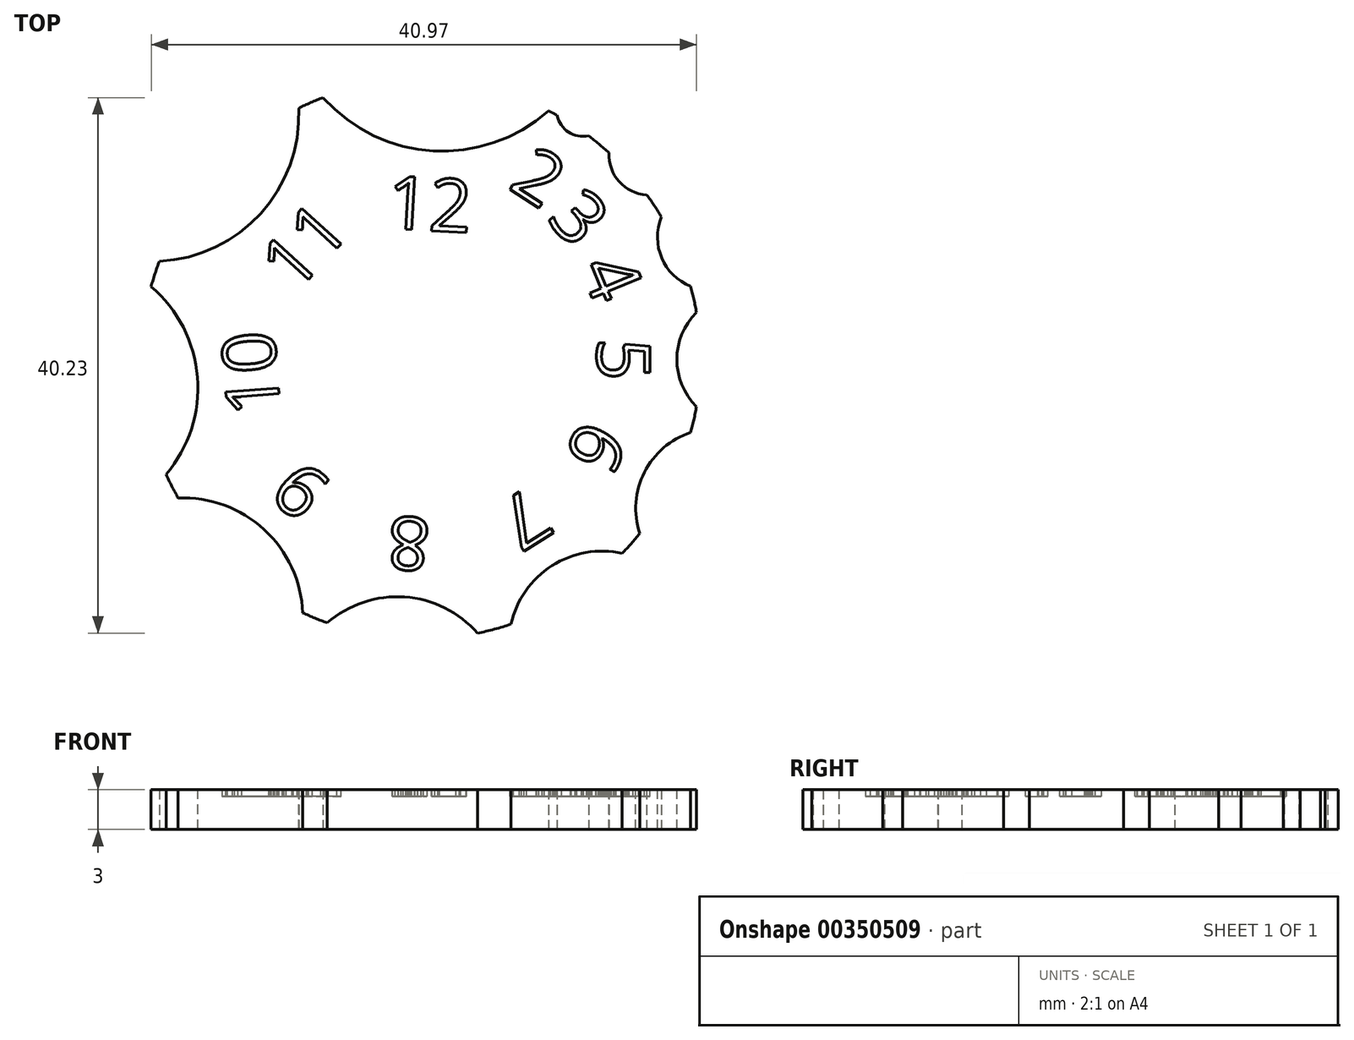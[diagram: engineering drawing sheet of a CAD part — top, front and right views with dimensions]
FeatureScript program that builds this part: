
annotation { "Feature Type Name" : "Feature", "Feature Type Description" : "" }
export const myFeature = defineFeature(function(context is Context, id is Id, definition is map)
    precondition{}
    {
        {
            assignVariable(context, id + "F0", {"name" : "max", "anyValue" : 10});
        }
        {
            var Q0;
            Q0=qCreatedBy(makeId("Top.planeOp"),FACE);
            var sketch = newSketch(context, id + "F1", { "sketchPlane" : qUnion([Q0])});
            skCircle(sketch, "E0", {"center": v(0, 0) * mm, "radius": 21 * mm});
            skSolve(sketch);
        }
        {
            var Q0;
            Q0=qCreatedBy(makeId("Top.planeOp"),FACE);
            var sketch = newSketch(context, id + "F2", { "sketchPlane" : qUnion([Q0])});
            skLineSegment(sketch, "E1", {"start": v(-20.27, 5.47) * mm, "end": v(-20.27, 5.47) * mm});
            skLineSegment(sketch, "E2", {"start": v(-19.15, -8.62) * mm, "end": v(-19.15, -8.62) * mm});
            skPoint(sketch, "E3.visualSharp", {"position": v(-12.66, -1.01) * mm});
            skLineSegment(sketch, "E4", {"start": v(-19.15, -8.62) * mm, "end": v(-18.24, -10.4) * mm});
            skLineSegment(sketch, "E5", {"start": v(-18.24, -10.4) * mm, "end": v(-9.25, -10.04) * mm});
            skLineSegment(sketch, "E6", {"start": v(-9.25, -10.04) * mm, "end": v(-8.88, -19.03) * mm});
            skLineSegment(sketch, "E7", {"start": v(-8.88, -19.03) * mm, "end": v(-7.03, -19.79) * mm});
            skLineSegment(sketch, "E8", {"start": v(-7.03, -19.79) * mm, "end": v(-1, -14.53) * mm});
            skLineSegment(sketch, "E9", {"start": v(-1, -14.53) * mm, "end": v(4.26, -20.56) * mm});
            skLineSegment(sketch, "E10", {"start": v(4.26, -20.56) * mm, "end": v(6.77, -19.88) * mm});
            skLineSegment(sketch, "E11", {"start": v(6.77, -19.88) * mm, "end": v(8.3, -13.05) * mm});
            skLineSegment(sketch, "E12", {"start": v(8.3, -13.05) * mm, "end": v(15.13, -14.57) * mm});
            skLineSegment(sketch, "E13", {"start": v(15.13, -14.57) * mm, "end": v(16.44, -13.06) * mm});
            skLineSegment(sketch, "E14", {"start": v(16.44, -13.06) * mm, "end": v(14.57, -7.36) * mm});
            skLineSegment(sketch, "E15", {"start": v(14.57, -7.36) * mm, "end": v(20.27, -5.49) * mm});
            skLineSegment(sketch, "E16", {"start": v(20.27, -5.49) * mm, "end": v(20.7, -3.54) * mm});
            skLineSegment(sketch, "E17", {"start": v(20.7, -3.54) * mm, "end": v(17.16, 0) * mm});
            skLineSegment(sketch, "E18", {"start": v(17.16, 0) * mm, "end": v(20.7, 3.54) * mm});
            skLineSegment(sketch, "E19", {"start": v(20.7, 3.54) * mm, "end": v(20.27, 5.49) * mm});
            skLineSegment(sketch, "E20", {"start": v(20.27, 5.49) * mm, "end": v(16.56, 7) * mm});
            skLineSegment(sketch, "E21", {"start": v(16.56, 7) * mm, "end": v(18.07, 10.7) * mm});
            skLineSegment(sketch, "E22", {"start": v(18.07, 10.7) * mm, "end": v(18.07, 10.7) * mm});
            skLineSegment(sketch, "E23", {"start": v(18.07, 10.7) * mm, "end": v(16.97, 12.37) * mm});
            skLineSegment(sketch, "E24", {"start": v(16.97, 12.37) * mm, "end": v(13.97, 12.53) * mm});
            skLineSegment(sketch, "E25", {"start": v(13.97, 12.53) * mm, "end": v(14.14, 15.53) * mm});
            skLineSegment(sketch, "E26", {"start": v(14.14, 15.53) * mm, "end": v(12.6, 16.8) * mm});
            skLineSegment(sketch, "E27", {"start": v(12.6, 16.8) * mm, "end": v(10.64, 16.39) * mm});
            skLineSegment(sketch, "E28", {"start": v(10.64, 16.39) * mm, "end": v(10.22, 18.34) * mm});
            skLineSegment(sketch, "E29", {"start": v(-20.27, 5.47) * mm, "end": v(-12.66, -1.01) * mm});
            skLineSegment(sketch, "E30", {"start": v(-12.66, -1.01) * mm, "end": v(-19.15, -8.62) * mm});
            skLineSegment(sketch, "E31", {"start": v(-20.27, 5.47) * mm, "end": v(-26.76, -2.14) * mm});
            skLineSegment(sketch, "E32", {"start": v(-26.76, -2.14) * mm, "end": v(-19.15, -8.62) * mm});
            skLineSegment(sketch, "E33", {"start": v(-18.24, -10.4) * mm, "end": v(-17.87, -19.4) * mm});
            skLineSegment(sketch, "E34", {"start": v(-17.87, -19.4) * mm, "end": v(-8.88, -19.03) * mm});
            skLineSegment(sketch, "E35", {"start": v(-7.03, -19.79) * mm, "end": v(-1.77, -25.82) * mm});
            skLineSegment(sketch, "E36", {"start": v(-1.77, -25.82) * mm, "end": v(4.26, -20.56) * mm});
            skLineSegment(sketch, "E37", {"start": v(6.77, -19.88) * mm, "end": v(13.6, -21.4) * mm});
            skLineSegment(sketch, "E38", {"start": v(13.6, -21.4) * mm, "end": v(15.13, -14.57) * mm});
            skLineSegment(sketch, "E39", {"start": v(16.44, -13.06) * mm, "end": v(22.14, -11.19) * mm});
            skLineSegment(sketch, "E40", {"start": v(22.14, -11.19) * mm, "end": v(20.27, -5.49) * mm});
            skLineSegment(sketch, "E41", {"start": v(20.7, -3.54) * mm, "end": v(24.24, 0) * mm});
            skLineSegment(sketch, "E42", {"start": v(24.24, 0) * mm, "end": v(20.7, 3.54) * mm});
            skLineSegment(sketch, "E43", {"start": v(20.27, 5.49) * mm, "end": v(21.78, 9.2) * mm});
            skLineSegment(sketch, "E44", {"start": v(21.78, 9.2) * mm, "end": v(18.07, 10.7) * mm});
            skLineSegment(sketch, "E45", {"start": v(16.97, 12.37) * mm, "end": v(17.13, 15.37) * mm});
            skLineSegment(sketch, "E46", {"start": v(17.13, 15.37) * mm, "end": v(14.14, 15.53) * mm});
            skLineSegment(sketch, "E47", {"start": v(12.6, 16.8) * mm, "end": v(12.18, 18.76) * mm});
            skLineSegment(sketch, "E48", {"start": v(12.18, 18.76) * mm, "end": v(10.22, 18.34) * mm});
            skLineSegment(sketch, "E49", {"start": v(-20.27, 5.47) * mm, "end": v(-19.66, 7.38) * mm});
            skLineSegment(sketch, "E50.bottom", {"start": v(-19.66, 7.38) * mm, "end": v(-8.67, 7.9) * mm});
            skLineSegment(sketch, "E50.top", {"start": v(-20.18, 18.37) * mm, "end": v(-9.19, 18.88) * mm});
            skLineSegment(sketch, "E50.left", {"start": v(-19.66, 7.38) * mm, "end": v(-20.18, 18.37) * mm});
            skLineSegment(sketch, "E50.right", {"start": v(-8.67, 7.9) * mm, "end": v(-9.19, 18.88) * mm});
            skLineSegment(sketch, "E51", {"start": v(-9.19, 18.88) * mm, "end": v(-7.35, 19.67) * mm});
            skLineSegment(sketch, "E52.bottom", {"start": v(-7.35, 19.67) * mm, "end": v(0.62, 10.7) * mm});
            skLineSegment(sketch, "E52.top", {"start": v(1.61, 27.65) * mm, "end": v(9.6, 18.68) * mm});
            skLineSegment(sketch, "E52.left", {"start": v(-7.35, 19.67) * mm, "end": v(1.61, 27.65) * mm});
            skLineSegment(sketch, "E52.right", {"start": v(0.62, 10.7) * mm, "end": v(9.6, 18.68) * mm});
            skSolve(sketch);
        }
        {
            var Q0;
            Q0 = qSketchRegion(id + "F1", true);
            extrude(context, id + "F3", {"entities" : qUnion([Q0]), "depth" : 3 * mm});
        }
        {
            var Q0;
            Q0 = qSketchRegion(id + "F2", true);
            extrude(context, id + "F4", {"entities" : qUnion([Q0]), "operationType" : NewBodyOperationType.REMOVE, "endBound" : BoundingType.THROUGH_ALL, "depth" : 25 * mm});
        }
        {
            var Q0;
            Q0=makeQuery(id+"F4.boolean.opBoolean","COPY",EDGE,{"derivedFrom":makeQuery(id+"F4.opExtrude","SWEPT_EDGE",EDGE,{"disambiguationData":[OSD([sQuery(id+"F2.wireOp",EDGE,"E29"),sQuery(id+"F2.wireOp",EDGE,"E30")])]})});
            fillet(context, id + "F5", {"entities" : qUnion([Q0]), "radius" : (getVariable(context, 'max')) * mm, "tangentPropagation" : true, "allowEdgeOverflow" : false});
        }
        {
            var Q0;
            Q0=makeQuery(id+"F4.boolean.opBoolean","COPY",EDGE,{"derivedFrom":makeQuery(id+"F4.opExtrude","SWEPT_EDGE",EDGE,{"disambiguationData":[OSD([sQuery(id+"F2.wireOp",EDGE,"E5"),sQuery(id+"F2.wireOp",EDGE,"E6")])]})});
            fillet(context, id + "F6", {"entities" : qUnion([Q0]), "radius" : (getVariable(context, 'max') - 1) * mm, "tangentPropagation" : true, "allowEdgeOverflow" : false});
        }
        {
            var Q0;
            Q0=makeQuery(id+"F4.boolean.opBoolean","COPY",EDGE,{"derivedFrom":makeQuery(id+"F4.opExtrude","SWEPT_EDGE",EDGE,{"disambiguationData":[OSD([sQuery(id+"F2.wireOp",EDGE,"E8"),sQuery(id+"F2.wireOp",EDGE,"E9")])]})});
            fillet(context, id + "F7", {"entities" : qUnion([Q0]), "radius" : (getVariable(context, 'max') - 2) * mm, "tangentPropagation" : true, "allowEdgeOverflow" : false});
        }
        {
            var Q0;
            Q0=makeQuery(id+"F4.boolean.opBoolean","COPY",EDGE,{"derivedFrom":makeQuery(id+"F4.opExtrude","SWEPT_EDGE",EDGE,{"disambiguationData":[OSD([sQuery(id+"F2.wireOp",EDGE,"E11"),sQuery(id+"F2.wireOp",EDGE,"E12")])]})});
            fillet(context, id + "F8", {"entities" : qUnion([Q0]), "radius" : (getVariable(context, 'max') - 3) * mm, "tangentPropagation" : true, "allowEdgeOverflow" : false});
        }
        {
            var Q0;
            Q0=makeQuery(id+"F4.boolean.opBoolean","COPY",EDGE,{"derivedFrom":makeQuery(id+"F4.opExtrude","SWEPT_EDGE",EDGE,{"disambiguationData":[OSD([sQuery(id+"F2.wireOp",EDGE,"E14"),sQuery(id+"F2.wireOp",EDGE,"E15")])]})});
            fillet(context, id + "F9", {"entities" : qUnion([Q0]), "radius" : (getVariable(context, 'max') - 4) * mm, "tangentPropagation" : true, "allowEdgeOverflow" : false});
        }
        {
            var Q0;
            Q0=makeQuery(id+"F4.boolean.opBoolean","COPY",EDGE,{"derivedFrom":makeQuery(id+"F4.opExtrude","SWEPT_EDGE",EDGE,{"disambiguationData":[OSD([sQuery(id+"F2.wireOp",EDGE,"E17"),sQuery(id+"F2.wireOp",EDGE,"E18")])]})});
            fillet(context, id + "F10", {"entities" : qUnion([Q0]), "radius" : (getVariable(context, 'max') - 5) * mm, "tangentPropagation" : true, "allowEdgeOverflow" : false});
        }
        {
            var Q0;
            Q0=makeQuery(id+"F4.boolean.opBoolean","COPY",EDGE,{"derivedFrom":makeQuery(id+"F4.opExtrude","SWEPT_EDGE",EDGE,{"disambiguationData":[OSD([sQuery(id+"F2.wireOp",EDGE,"E20"),sQuery(id+"F2.wireOp",EDGE,"E21")])]})});
            fillet(context, id + "F11", {"entities" : qUnion([Q0]), "radius" : (getVariable(context, 'max') - 6) * mm, "tangentPropagation" : true, "allowEdgeOverflow" : false});
        }
        {
            var Q0;
            Q0=makeQuery(id+"F4.boolean.opBoolean","COPY",EDGE,{"derivedFrom":makeQuery(id+"F4.opExtrude","SWEPT_EDGE",EDGE,{"disambiguationData":[OSD([sQuery(id+"F2.wireOp",EDGE,"E24"),sQuery(id+"F2.wireOp",EDGE,"E25")])]})});
            fillet(context, id + "F12", {"entities" : qUnion([Q0]), "radius" : (getVariable(context, 'max') - 7) * mm, "tangentPropagation" : true, "allowEdgeOverflow" : false});
        }
        {
            var Q0;
            Q0=makeQuery(id+"F4.boolean.opBoolean","COPY",EDGE,{"derivedFrom":makeQuery(id+"F4.opExtrude","SWEPT_EDGE",EDGE,{"disambiguationData":[OSD([sQuery(id+"F2.wireOp",EDGE,"E27"),sQuery(id+"F2.wireOp",EDGE,"E28")])]})});
            fillet(context, id + "F13", {"entities" : qUnion([Q0]), "radius" : (getVariable(context, 'max') - 8) * mm, "tangentPropagation" : true, "allowEdgeOverflow" : false});
        }
        {
            var Q0;
            Q0=makeQuery(id+"F4.boolean.opBoolean","COPY",EDGE,{"derivedFrom":makeQuery(id+"F4.opExtrude","SWEPT_EDGE",EDGE,{"disambiguationData":[OSD([sQuery(id+"F2.wireOp",EDGE,"E50.bottom"),sQuery(id+"F2.wireOp",EDGE,"E50.right")])]})});
            fillet(context, id + "F14", {"entities" : qUnion([Q0]), "radius" : (getVariable(context, 'max') + 1) * mm, "tangentPropagation" : true, "allowEdgeOverflow" : false});
        }
        {
            var Q0;
            Q0=makeQuery(id+"F4.boolean.opBoolean","COPY",EDGE,{"derivedFrom":makeQuery(id+"F4.opExtrude","SWEPT_EDGE",EDGE,{"disambiguationData":[OSD([sQuery(id+"F2.wireOp",EDGE,"E52.bottom"),sQuery(id+"F2.wireOp",EDGE,"E52.right")])]})});
            fillet(context, id + "F15", {"entities" : qUnion([Q0]), "radius" : (getVariable(context, 'max') + 2) * mm, "tangentPropagation" : true, "allowEdgeOverflow" : false});
        }
        {
            var Q0;
            Q0=makeQuery(id+"F3.opExtrude","CAP_FACE",FACE,{"disambiguationData":[OSD([sQuery(id+"F1.wireOp",EDGE,"E0")])],"isStart":false});
            var sketch = newSketch(context, id + "F16", { "sketchPlane" : qUnion([Q0])});
            skLineSegment(sketch, "E53", {"start": v(0.91, 15.67) * mm, "end": v(0.8, 13.67) * mm});
            skText(sketch, "E54", { "text": "12", "fontName": "OpenSans-Regular.ttf"});
            skText(sketch, "E55", { "text": "11", "fontName": "OpenSans-Regular.ttf"});
            skLineSegment(sketch, "E56", {"start": v(-10.56, 9.62) * mm, "end": v(-12.04, 10.96) * mm});
            skText(sketch, "E57", { "text": "10", "fontName": "OpenSans-Regular.ttf"});
            skLineSegment(sketch, "E58", {"start": v(-14.8, -1.18) * mm, "end": v(-16.8, -1.34) * mm});
            skText(sketch, "E59", { "text": "9", "fontName": "OpenSans-Regular.ttf"});
            skLineSegment(sketch, "E60", {"start": v(-10.42, -11.3) * mm, "end": v(-11.77, -12.78) * mm});
            skText(sketch, "E61", { "text": "8", "fontName": "OpenSans-Regular.ttf"});
            skLineSegment(sketch, "E62", {"start": v(-1.23, -17.84) * mm, "end": v(-1.09, -15.84) * mm});
            skLineSegment(sketch, "E63", {"start": v(9.85, -15.5) * mm, "end": v(8.84, -13.77) * mm});
            skText(sketch, "E64", { "text": "7", "fontName": "OpenSans-Regular.ttf"});
            skText(sketch, "E65", { "text": "6", "fontName": "OpenSans-Regular.ttf"});
            skText(sketch, "E66", { "text": "5", "fontName": "OpenSans-Regular.ttf"});
            skText(sketch, "E67", { "text": "4", "fontName": "OpenSans-Regular.ttf"});
            skText(sketch, "E68", { "text": "3", "fontName": "OpenSans-Regular.ttf"});
            skText(sketch, "E69", { "text": "2", "fontName": "OpenSans-Regular.ttf"});
            skLineSegment(sketch, "E70", {"start": v(16.79, -8.48) * mm, "end": v(15, -7.58) * mm});
            skLineSegment(sketch, "E71", {"start": v(18.1, 7.64) * mm, "end": v(16.25, 6.86) * mm});
            skLineSegment(sketch, "E72", {"start": v(14.9, 13.36) * mm, "end": v(13.41, 12.03) * mm});
            skLineSegment(sketch, "E73", {"start": v(11.1, 17.08) * mm, "end": v(10, 15.4) * mm});
            skLineSegment(sketch, "E74", {"start": v(19.24, 0) * mm, "end": v(17.24, 0) * mm});
            const initialGuessF16  = {"E54": [-0.00264, 0.00987, 0.9983, -0.05828, 0.004], "E55": [-0.00945, 0.0049, 0.67314, 0.73951, 0.004], "E57": [-0.01055, -0.00407, -0.0796, 0.99683, 0.004], "E59": [-0.00652, -0.00946, -0.7354, 0.67763, 0.004], "E61": [0.0008, -0.01196, -0.99765, 0.06857, 0.004], "E64": [0.00804, -0.00952, -0.8416, -0.54012, 0.004], "E65": [0.01217, -0.00432, -0.45099, -0.89253, 0.004], "E66": [0.01324, 0.0016, 0, -1, 0.004], "E67": [0.0119, 0.00688, 0.389, -0.92124, 0.004], "E68": [0.00936, 0.01055, 0.66769, -0.74444, 0.004], "E69": [0.00646, 0.01293, 0.83873, -0.54454, 0.004]};
            skSetInitialGuess(sketch, initialGuessF16);
            skSolve(sketch);
        }
        {
            var Q0;
            Q0 = qSketchRegion(id + "F16", true);
            extrude(context, id + "F17", {"entities" : qUnion([Q0]), "operationType" : NewBodyOperationType.REMOVE, "oppositeDirection" : true, "depth" : .50 * mm});
        }
    });
